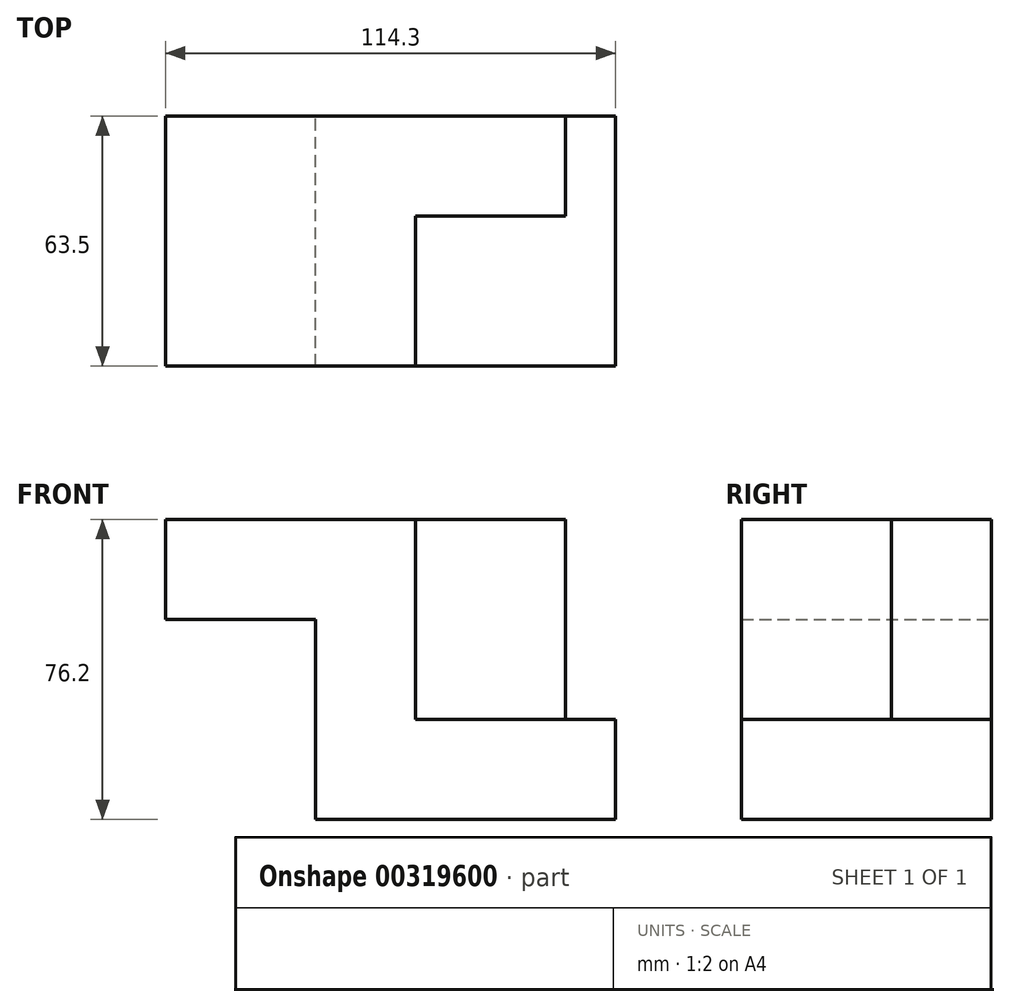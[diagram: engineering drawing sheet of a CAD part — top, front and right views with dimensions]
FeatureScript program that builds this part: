
annotation { "Feature Type Name" : "Feature", "Feature Type Description" : "" }
export const myFeature = defineFeature(function(context is Context, id is Id, definition is map)
    precondition{}
    {
        {
            var Q0;
            Q0=qCreatedBy(makeId("Front.planeOp"),FACE);
            var sketch = newSketch(context, id + "F0", { "sketchPlane" : qUnion([Q0])});
            skLineSegment(sketch, "E0", {"start": v(-16.38, -22.13) * mm, "end": v(59.82, -22.13) * mm});
            skLineSegment(sketch, "E1", {"start": v(59.82, -22.13) * mm, "end": v(59.82, 3.27) * mm});
            skLineSegment(sketch, "E2", {"start": v(59.82, 3.27) * mm, "end": v(9.02, 3.27) * mm});
            skLineSegment(sketch, "E3", {"start": v(9.02, 3.27) * mm, "end": v(9.02, 54.07) * mm});
            skLineSegment(sketch, "E4", {"start": v(9.02, 54.07) * mm, "end": v(-54.48, 54.07) * mm});
            skLineSegment(sketch, "E5", {"start": v(-54.48, 54.07) * mm, "end": v(-54.48, 28.67) * mm});
            skLineSegment(sketch, "E6", {"start": v(-54.48, 28.67) * mm, "end": v(-16.38, 28.67) * mm});
            skLineSegment(sketch, "E7", {"start": v(-16.38, 28.67) * mm, "end": v(-16.38, -22.13) * mm});
            skSolve(sketch);
        }
        {
            var Q0;
            Q0=makeQuery(id+"F0.imprint","IMPRINT",FACE,{"disambiguationData":[TD([[makeQuery(id+"F0.imprint","IMPRINT",EDGE,{"derivedFrom":sQuery(id+"F0.wireOp",EDGE,"E0")}),1.0]])]});
            extrude(context, id + "F1", {"entities" : qUnion([Q0]), "depth" : 63.5 * mm});
        }
        {
            var Q0;
            Q0=makeQuery(id+"F1.opExtrude","CAP_FACE",FACE,{"disambiguationData":[OSD([sQuery(id+"F0.wireOp",EDGE,"E0"),sQuery(id+"F0.wireOp",EDGE,"E1"),sQuery(id+"F0.wireOp",EDGE,"E2"),sQuery(id+"F0.wireOp",EDGE,"E3"),sQuery(id+"F0.wireOp",EDGE,"E4"),sQuery(id+"F0.wireOp",EDGE,"E5"),sQuery(id+"F0.wireOp",EDGE,"E6"),sQuery(id+"F0.wireOp",EDGE,"E7")])],"isStart":true});
            var sketch = newSketch(context, id + "F2", { "sketchPlane" : qUnion([Q0])});
            skLineSegment(sketch, "E8", {"start": v(-9.02, 54.07) * mm, "end": v(-47.12, 54.07) * mm});
            skLineSegment(sketch, "E9", {"start": v(-47.12, 54.07) * mm, "end": v(-47.12, 3.27) * mm});
            skLineSegment(sketch, "E10", {"start": v(-47.12, 3.27) * mm, "end": v(-9.02, 3.27) * mm});
            skLineSegment(sketch, "E11", {"start": v(-9.02, 3.27) * mm, "end": v(-9.02, 54.07) * mm});
            skSolve(sketch);
        }
        {
            var Q0;
            Q0=makeQuery(id+"F2.imprint","IMPRINT",FACE,{"disambiguationData":[TD([[makeQuery(id+"F2.imprint","IMPRINT",EDGE,{"derivedFrom":sQuery(id+"F2.wireOp",EDGE,"E8")}),1.0]])]});
            extrude(context, id + "F3", {"entities" : qUnion([Q0]), "operationType" : NewBodyOperationType.ADD, "oppositeDirection" : true, "depth" : 25.4 * mm});
        }
    });
